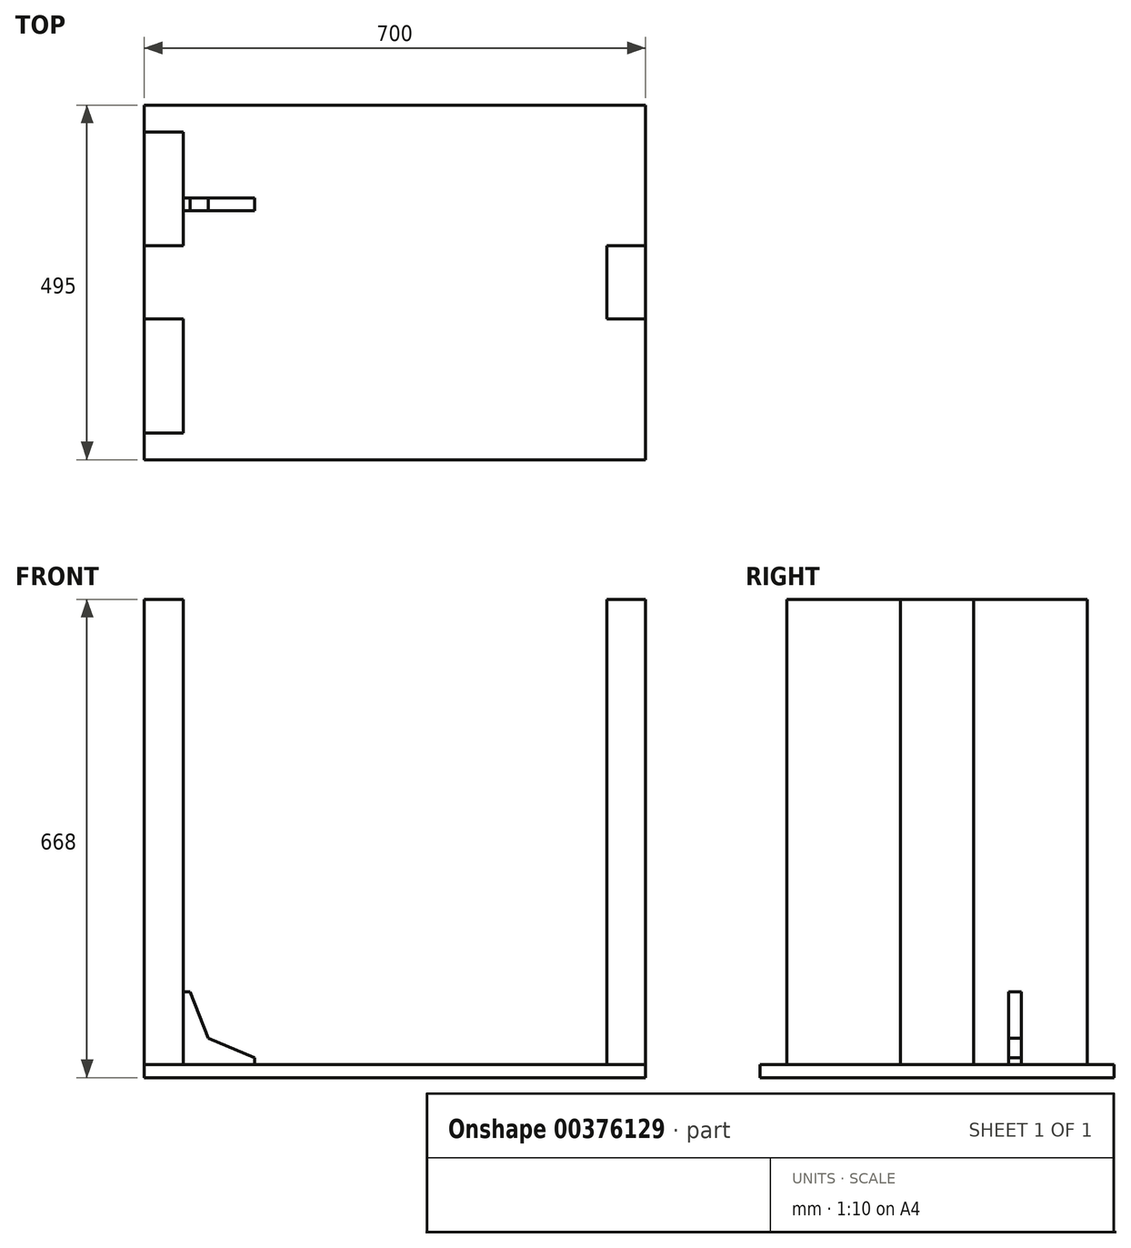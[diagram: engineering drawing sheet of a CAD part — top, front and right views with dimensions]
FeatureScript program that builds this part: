
annotation { "Feature Type Name" : "Feature", "Feature Type Description" : "" }
export const myFeature = defineFeature(function(context is Context, id is Id, definition is map)
    precondition{}
    {
        {
            var Q0;
            Q0=qCreatedBy(makeId("Top.planeOp"),FACE);
            var sketch = newSketch(context, id + "F0", { "sketchPlane" : qUnion([Q0])});
            skLineSegment(sketch, "E0.bottom", {"start": v(-350, 247.5) * mm, "end": v(350, 247.5) * mm});
            skLineSegment(sketch, "E0.top", {"start": v(-350, -247.5) * mm, "end": v(350, -247.5) * mm});
            skLineSegment(sketch, "E0.left", {"start": v(-350, 247.5) * mm, "end": v(-350, -247.5) * mm});
            skLineSegment(sketch, "E0.right", {"start": v(350, 247.5) * mm, "end": v(350, -247.5) * mm});
            skPoint(sketch, "E1", {"position": v(0, 247.5) * mm});
            skPoint(sketch, "E2", {"position": v(-350, 0) * mm});
            skSolve(sketch);
        }
        {
            var Q0;
            Q0=qSketchRegion(id+"F0",true);
            extrude(context, id + "F1", {"entities" : qUnion([Q0]), "depth" : 18 * mm, "offsetDistance" : 25 * mm});
        }
        {
            var Q0;
            Q0=makeQuery(id+"F1.opExtrude","CAP_FACE",FACE,{"disambiguationData":[OSD([sQuery(id+"F0.wireOp",EDGE,"E0.bottom"),sQuery(id+"F0.wireOp",EDGE,"E0.top"),sQuery(id+"F0.wireOp",EDGE,"E0.left"),sQuery(id+"F0.wireOp",EDGE,"E0.right")])],"isStart":false});
            var sketch = newSketch(context, id + "F2", { "sketchPlane" : qUnion([Q0])});
            skPoint(sketch, "E3", {"position": v(-350, 0) * mm});
            skLineSegment(sketch, "E4.bottom", {"start": v(-350, 210) * mm, "end": v(-296, 210) * mm});
            skLineSegment(sketch, "E4.top", {"start": v(-350, -210) * mm, "end": v(-296, -210) * mm});
            skLineSegment(sketch, "E4.left", {"start": v(-350, 210) * mm, "end": v(-350, -210) * mm});
            skLineSegment(sketch, "E4.right", {"start": v(-296, 210) * mm, "end": v(-296, -210) * mm});
            skLineSegment(sketch, "E5.bottom", {"start": v(350, -51) * mm, "end": v(296, -51) * mm});
            skLineSegment(sketch, "E5.top", {"start": v(350, 51) * mm, "end": v(296, 51) * mm});
            skLineSegment(sketch, "E5.left", {"start": v(350, -51) * mm, "end": v(350, 51) * mm});
            skLineSegment(sketch, "E5.right", {"start": v(296, -51) * mm, "end": v(296, 51) * mm});
            skPoint(sketch, "E6", {"position": v(350, 0) * mm});
            skPoint(sketch, "E7", {"position": v(0, -247.5) * mm});
            skSolve(sketch);
        }
        {
            var Q0;
            {var subQ1=sQuery(id+"F2.wireOp",EDGE,"E4.bottom");Q0=makeQuery(id+"F2.imprint","IMPRINT",FACE,{"disambiguationData":[TD([[makeQuery(id+"F2.imprint","IMPRINT",EDGE,{"derivedFrom":subQ1}),-1.0]])]});}
            var Q1;
            Q1=makeQuery(id+"F2.imprint","IMPRINT",FACE,{"disambiguationData":[TD([[makeQuery(id+"F2.imprint","IMPRINT",EDGE,{"derivedFrom":sQuery(id+"F2.wireOp",EDGE,"1kVaZgk3-8Nhi-dGg9-Ba8R-nr3TmBuge7lK.bottom")}),-1.0]])]});
            var Q2;
            Q2=makeQuery(id+"F2.imprint","IMPRINT",FACE,{"disambiguationData":[TD([[makeQuery(id+"F2.imprint","IMPRINT",EDGE,{"derivedFrom":sQuery(id+"F2.wireOp",EDGE,"d1aede41-c4be-4dbf-9319-fc5a6116a92b.bottom")}),-1.0]])]});
            var Q3;
            {var subQ1=sQuery(id+"F2.wireOp",EDGE,"E5.bottom");Q3=makeQuery(id+"F2.imprint","IMPRINT",FACE,{"disambiguationData":[TD([[makeQuery(id+"F2.imprint","IMPRINT",EDGE,{"derivedFrom":subQ1}),-1.0]])]});}
            extrude(context, id + "F3", {"entities" : qUnion([Q0, Q1, Q2, Q3]), "depth" : 650 * mm, "offsetDistance" : 25 * mm});
        }
        {
            var Q0;
            Q0=makeQuery(id+"F3.opExtrude","SWEPT_FACE",FACE,{"disambiguationData":[OSD([sQuery(id+"F2.wireOp",EDGE,"E5.left")])]});
            var sketch = newSketch(context, id + "F4", { "sketchPlane" : qUnion([Q0])});
            skLineSegment(sketch, "E8.bottom", {"start": v(51, 18) * mm, "end": v(-51, 18) * mm});
            skLineSegment(sketch, "E8.top", {"start": v(51, 668) * mm, "end": v(-51, 668) * mm});
            skLineSegment(sketch, "E8.left", {"start": v(51, 18) * mm, "end": v(51, 668) * mm});
            skLineSegment(sketch, "E8.right", {"start": v(-51, 18) * mm, "end": v(-51, 668) * mm});
            skPoint(sketch, "E9", {"position": v(0, 18) * mm});
            skPoint(sketch, "E10", {"position": v(140, 18) * mm});
            skPoint(sketch, "E11", {"position": v(-140, 18) * mm});
            skPoint(sketch, "E12", {"position": v(140, 668) * mm});
            skPoint(sketch, "E13", {"position": v(-140, 668) * mm});
            skLineSegment(sketch, "E14", {"start": v(51, 18) * mm, "end": v(140, 668) * mm});
            skLineSegment(sketch, "E15", {"start": v(-140, 668) * mm, "end": v(-51, 18) * mm});
            skSolve(sketch);
        }
        {
            var Q0;
            {var subQ0=sQuery(id+"F4.wireOp",EDGE,"E8.left");Q0=makeQuery(id+"F4.imprint","IMPRINT",FACE,{"disambiguationData":[TD([[makeQuery(id+"F4.imprint","IMPRINT",EDGE,{"derivedFrom":subQ0}),-1.0]])]});}
            var Q1;
            {var subQ0=sQuery(id+"F4.wireOp",EDGE,"E8.right");Q1=makeQuery(id+"F4.imprint","IMPRINT",FACE,{"disambiguationData":[TD([[makeQuery(id+"F4.imprint","IMPRINT",EDGE,{"derivedFrom":subQ0}),1.0]])]});}
            var Q2;
            {var subQ3=sQuery(id+"F4.wireOp",EDGE,"ERWEisdO-8PsZ-Fccj-wROh-Rmm69zbihmoK");Q2=makeQuery(id+"F4.imprint","IMPRINT",FACE,{"disambiguationData":[TD([[makeQuery(id+"F4.imprint","IMPRINT",EDGE,{"derivedFrom":subQ3}),-1.0]])]});}
            var Q3;
            {var subQ3=sQuery(id+"F4.wireOp",EDGE,"njEO2kw1-x9P7-cku3-6qRM-CGIWQrq0eT6F");Q3=makeQuery(id+"F4.imprint","IMPRINT",FACE,{"disambiguationData":[TD([[makeQuery(id+"F4.imprint","IMPRINT",EDGE,{"derivedFrom":subQ3}),1.0]])]});}
            var Q4;
            {var subQ0=sQuery(id+"F4.wireOp",EDGE,"ERWEisdO-8PsZ-Fccj-wROh-Rmm69zbihmoK");Q4=makeQuery(id+"F4.imprint","IMPRINT",FACE,{"disambiguationData":[TD([[makeQuery(id+"F4.imprint","IMPRINT",EDGE,{"derivedFrom":subQ0}),1.0]])]});}
            var Q5;
            {var subQ0=sQuery(id+"F4.wireOp",EDGE,"njEO2kw1-x9P7-cku3-6qRM-CGIWQrq0eT6F");Q5=makeQuery(id+"F4.imprint","IMPRINT",FACE,{"disambiguationData":[TD([[makeQuery(id+"F4.imprint","IMPRINT",EDGE,{"derivedFrom":subQ0}),-1.0]])]});}
            extrude(context, id + "F5", {"entities" : qUnion([Q0, Q1, Q2, Q3, Q4, Q5]), "operationType" : NewBodyOperationType.REMOVE, "endBound" : BoundingType.THROUGH_ALL, "oppositeDirection" : true, "depth" : 25 * mm, "offsetDistance" : 25 * mm});
        }
        {
            var Q0;
            Q0=makeQuery(id+"F3.opExtrude","SWEPT_FACE",FACE,{"disambiguationData":[OSD([sQuery(id+"F2.wireOp",EDGE,"E4.right"),sQuery(id+"F2.wireOp",EDGE,"1kVaZgk3-8Nhi-dGg9-Ba8R-nr3TmBuge7lK.left")])]});
            var sketch = newSketch(context, id + "F6", { "sketchPlane" : qUnion([Q0])});
            skLineSegment(sketch, "E16.bottom", {"start": v(118, 18) * mm, "end": v(100, 18) * mm});
            skLineSegment(sketch, "E16.top", {"start": v(118, 120) * mm, "end": v(100, 120) * mm});
            skLineSegment(sketch, "E16.left", {"start": v(118, 18) * mm, "end": v(118, 120) * mm});
            skLineSegment(sketch, "E16.right", {"start": v(100, 18) * mm, "end": v(100, 120) * mm});
            skSolve(sketch);
        }
        {
            var Q0;
            Q0=makeQuery(id+"F6.imprint","IMPRINT",FACE,{"disambiguationData":[TD([[makeQuery(id+"F6.imprint","IMPRINT",EDGE,{"derivedFrom":sQuery(id+"F6.wireOp",EDGE,"E16.bottom")}),-1.0]])]});
            extrude(context, id + "F7", {"entities" : qUnion([Q0]), "depth" : 100 * mm, "offsetDistance" : 25 * mm});
        }
        {
            var Q0;
            {var subQ1=sQuery(id+"F2.wireOp",EDGE,"E5.bottom");Q0=makeQuery(id+"F2.imprint","IMPRINT",FACE,{"disambiguationData":[TD([[makeQuery(id+"F2.imprint","IMPRINT",EDGE,{"derivedFrom":subQ1}),-1.0]])]});}
            extrude(context, id + "F8", {"entities" : qUnion([Q0]), "depth" : 650 * mm, "offsetDistance" : 25 * mm});
        }
        {
            var Q0;
            Q0=makeQuery(id+"F7.opExtrude","SWEPT_FACE",FACE,{"disambiguationData":[OSD([sQuery(id+"F6.wireOp",EDGE,"E16.left")])]});
            var sketch = newSketch(context, id + "F9", { "sketchPlane" : qUnion([Q0])});
            skLineSegment(sketch, "E17", {"start": v(312.75, 72.54) * mm, "end": v(267.75, 72.54) * mm});
            skLineSegment(sketch, "E18", {"start": v(322.73, 98.5) * mm, "end": v(277.73, 98.5) * mm});
            skLineSegment(sketch, "E19", {"start": v(251.8, 6.18) * mm, "end": v(251.8, 51.18) * mm});
            skLineSegment(sketch, "E20", {"start": v(211.36, 9.38) * mm, "end": v(211.36, 34.38) * mm});
            skLineSegment(sketch, "E21", {"start": v(286, 120) * mm, "end": v(261, 55) * mm});
            skLineSegment(sketch, "E22", {"start": v(261, 55) * mm, "end": v(196, 28) * mm});
            skLineSegment(sketch, "E23.bottom", {"start": v(296, 18) * mm, "end": v(196, 18) * mm});
            skLineSegment(sketch, "E23.top", {"start": v(251, 120) * mm, "end": v(196, 120) * mm});
            skLineSegment(sketch, "E23.left", {"start": v(296, 18) * mm, "end": v(296, 120) * mm});
            skLineSegment(sketch, "E23.right", {"start": v(196, 18) * mm, "end": v(196, 120) * mm});
            skSolve(sketch);
        }
        {
            var Q0;
            {var subQ2=sQuery(id+"F9.wireOp",EDGE,"E21");var subQ4=makeQuery(id+"F9.imprint","INTERSECT",VERTEX,{"derivedFrom":[sQuery(id+"F9.wireOp",EDGE,"E17"),subQ2]});Q0=makeQuery(id+"F9.imprint","IMPRINT",FACE,{"disambiguationData":[TD([[makeQuery(id+"F9.imprint","IMPRINT",EDGE,{"disambiguationData":[TD([[subQ4,1.0]])],"derivedFrom":subQ2}),-1.0]])]});}
            extrude(context, id + "F10", {"entities" : qUnion([Q0]), "operationType" : NewBodyOperationType.REMOVE, "oppositeDirection" : true, "depth" : 25 * mm});
        }
    });
